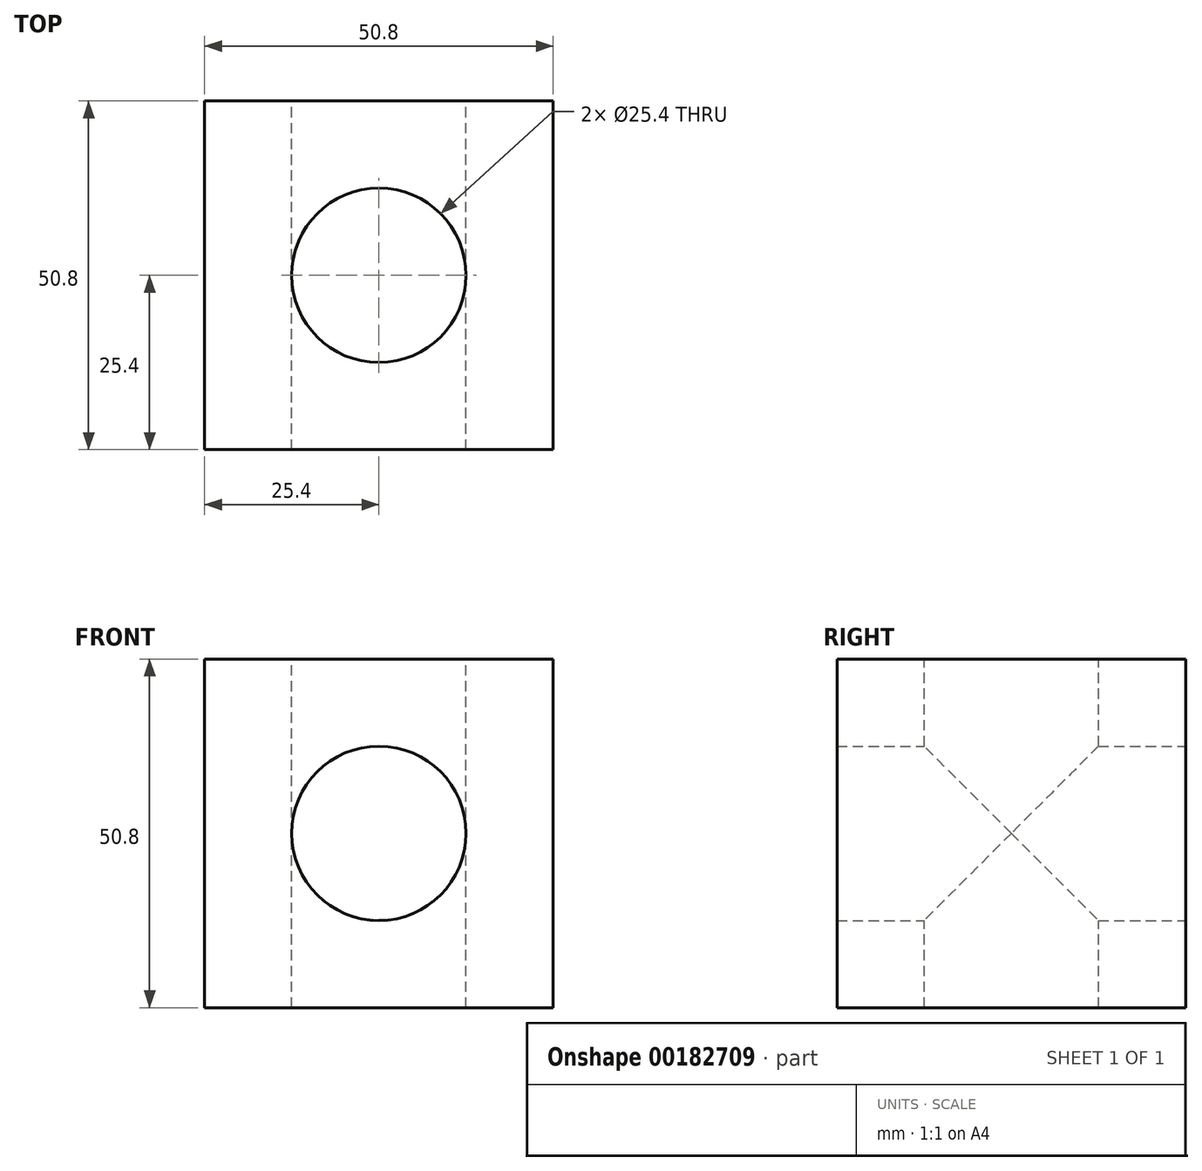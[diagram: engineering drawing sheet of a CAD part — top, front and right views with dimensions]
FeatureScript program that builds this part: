
annotation { "Feature Type Name" : "Feature", "Feature Type Description" : "" }
export const myFeature = defineFeature(function(context is Context, id is Id, definition is map)
    precondition{}
    {
        {
            var Q0;
            Q0=qCreatedBy(makeId("Right.planeOp"),FACE);
            var sketch = newSketch(context, id + "F0", { "sketchPlane" : qUnion([Q0])});
            skLineSegment(sketch, "E0.bottom", {"start": v(-25.4, 25.4) * mm, "end": v(25.4, 25.4) * mm});
            skLineSegment(sketch, "E0.top", {"start": v(-25.4, -25.4) * mm, "end": v(25.4, -25.4) * mm});
            skLineSegment(sketch, "E0.left", {"start": v(-25.4, 25.4) * mm, "end": v(-25.4, -25.4) * mm});
            skLineSegment(sketch, "E0.right", {"start": v(25.4, 25.4) * mm, "end": v(25.4, -25.4) * mm});
            skPoint(sketch, "E0.middle", {"position": v(0, 0) * mm});
            skCircle(sketch, "E1", {"center": v(0, 0) * mm, "radius": 12.7 * mm});
            skSolve(sketch);
        }
        {
            var Q0;
            Q0=makeQuery(id+"F0.imprint","IMPRINT",FACE,{"disambiguationData":[TD([[makeQuery(id+"F0.imprint","IMPRINT",EDGE,{"derivedFrom":sQuery(id+"F0.wireOp",EDGE,"E1")}),1.0]])]});
            var Q1;
            Q1=makeQuery(id+"F0.imprint","IMPRINT",FACE,{"disambiguationData":[TD([[makeQuery(id+"F0.imprint","IMPRINT",EDGE,{"derivedFrom":sQuery(id+"F0.wireOp",EDGE,"E0.bottom")}),-1.0]])]});
            extrude(context, id + "F1", {"entities" : qUnion([Q0, Q1]), "depth" : 50.8 * mm});
        }
        {
            var Q0;
            Q0=makeQuery(id+"F1.opExtrude","SWEPT_FACE",FACE,{"disambiguationData":[OSD([sQuery(id+"F0.wireOp",EDGE,"E0.right")])]});
            var sketch = newSketch(context, id + "F2", { "sketchPlane" : qUnion([Q0])});
            skPoint(sketch, "E2.centerSnap0", {"position": v(-50.8, 0) * mm});
            skCircle(sketch, "E3", {"center": v(-25.4, 0) * mm, "radius": 12.7 * mm});
            skSolve(sketch);
        }
        {
            var Q0;
            Q0=sQuery(id+"F2.wireOp",VERTEX,"E3.center");
            var Q1;
            Q1=makeQuery(id+"F1.opExtrude","SWEPT_BODY",BODY,{"disambiguationData":[OSD([sQuery(id+"F0.wireOp",EDGE,"E0.bottom"),sQuery(id+"F0.wireOp",EDGE,"E0.top"),sQuery(id+"F0.wireOp",EDGE,"E0.left"),sQuery(id+"F0.wireOp",EDGE,"E0.right")])]});
            hole(context, id + "F3", {"style" : HoleStyle.SIMPLE, "endStyle" : HoleEndStyle.THROUGH, "holeDiameter" : 25.4 * mm, "locations" : qUnion([Q0]), "scope" : qUnion([Q1]), "isTappedThrough" : true});
        }
        {
            var Q0;
            Q0=makeQuery(id+"F1.opExtrude","SWEPT_FACE",FACE,{"disambiguationData":[OSD([sQuery(id+"F0.wireOp",EDGE,"E0.bottom")])]});
            var sketch = newSketch(context, id + "F4", { "sketchPlane" : qUnion([Q0])});
            skLineSegment(sketch, "E4", {"start": v(50.8, 0) * mm, "end": v(0, 0) * mm});
            skLineSegment(sketch, "E5", {"start": v(25.4, -25.4) * mm, "end": v(25.4, 25.4) * mm});
            skCircle(sketch, "E6", {"center": v(25.4, 0) * mm, "radius": 12.7 * mm});
            skSolve(sketch);
        }
        {
            var Q0;
            Q0=sQuery(id+"F4.wireOp",VERTEX,"E6.center");
            var Q1;
            Q1=makeQuery(id+"F1.opExtrude","SWEPT_BODY",BODY,{"disambiguationData":[OSD([sQuery(id+"F0.wireOp",EDGE,"E0.bottom"),sQuery(id+"F0.wireOp",EDGE,"E0.top"),sQuery(id+"F0.wireOp",EDGE,"E0.left"),sQuery(id+"F0.wireOp",EDGE,"E0.right")])]});
            hole(context, id + "F5", {"style" : HoleStyle.SIMPLE, "endStyle" : HoleEndStyle.THROUGH, "holeDiameter" : 25.4 * mm, "locations" : qUnion([Q0]), "scope" : qUnion([Q1]), "isTappedThrough" : true});
        }
        {
            var Q0;
            Q0=makeQuery(id+"F1.opExtrude","CAP_FACE",FACE,{"disambiguationData":[OSD([sQuery(id+"F0.wireOp",EDGE,"E0.bottom"),sQuery(id+"F0.wireOp",EDGE,"E0.top"),sQuery(id+"F0.wireOp",EDGE,"E0.left"),sQuery(id+"F0.wireOp",EDGE,"E0.right")])],"isStart":false});
            var sketch = newSketch(context, id + "F6", { "sketchPlane" : qUnion([Q0])});
            skCircle(sketch, "E7", {"center": v(0, 0) * mm, "radius": 12.7 * mm});
            skSolve(sketch);
        }
        {
            var Q0;
            Q0=sQuery(id+"F6.wireOp",EDGE,"E7");
            extrude(context, id + "F7", {"bodyType" : ToolBodyType.SURFACE, "surfaceEntities" : qUnion([Q0]), "depth" : 25.4 * mm});
        }
    });
